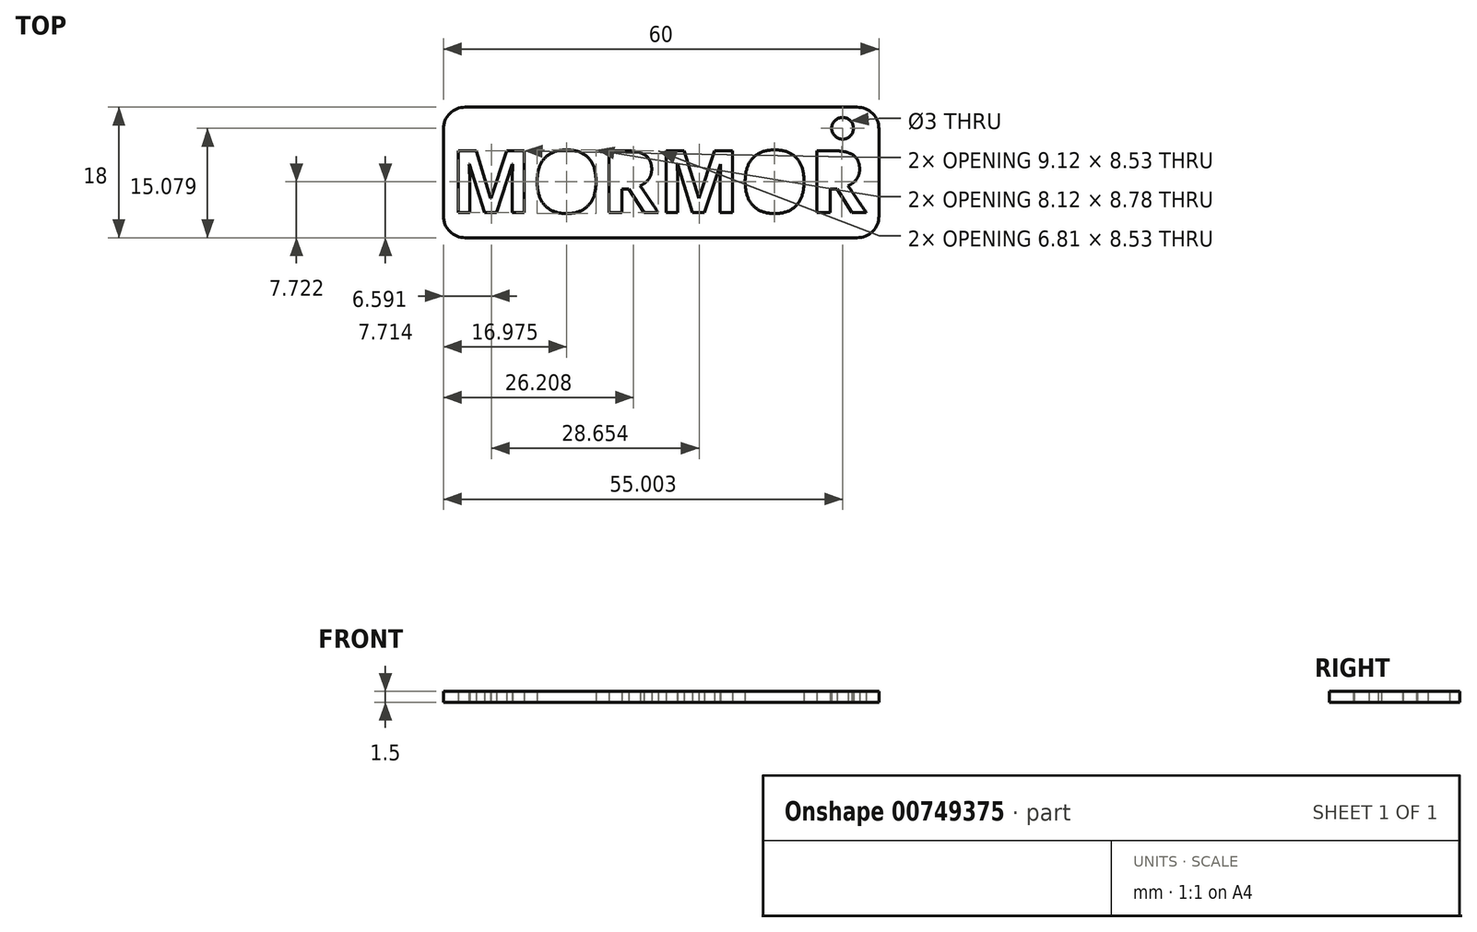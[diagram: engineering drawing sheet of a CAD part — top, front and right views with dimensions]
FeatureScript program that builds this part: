
annotation { "Feature Type Name" : "Feature", "Feature Type Description" : "" }
export const myFeature = defineFeature(function(context is Context, id is Id, definition is map)
    precondition{}
    {
        {
            var Q0;
            Q0=qCreatedBy(makeId("Top.planeOp"),FACE);
            var sketch = newSketch(context, id + "F0", { "sketchPlane" : qUnion([Q0])});
            skLineSegment(sketch, "E0.bottom", {"start": v(-26.45, -7.35) * mm, "end": v(33.55, -7.35) * mm});
            skLineSegment(sketch, "E0.top", {"start": v(-26.45, -25.35) * mm, "end": v(33.55, -25.35) * mm});
            skLineSegment(sketch, "E0.left", {"start": v(-26.45, -7.35) * mm, "end": v(-26.45, -25.35) * mm});
            skLineSegment(sketch, "E0.right", {"start": v(33.55, -7.35) * mm, "end": v(33.55, -25.35) * mm});
            skLineSegment(sketch, "E1", {"start": v(-21.45, -7.35) * mm, "end": v(-21.45, -25.35) * mm, "construction": true});
            skLineSegment(sketch, "E2", {"start": v(28.55, -7.35) * mm, "end": v(28.55, -25.35) * mm, "construction": true});
            skCircle(sketch, "E3", {"center": v(28.55, -10.27) * mm, "radius": 1.5 * mm});
            skText(sketch, "E4", { "text": "MORMOR", "fontName": "OpenSans-Bold.ttf"});
            skPoint(sketch, "E5", {"position": v(3.55, -25.35) * mm});
            const initialGuessF0  = {"E4": [-0.02549, -0.0219, 1, 0, 0.0086]};
            skSetInitialGuess(sketch, initialGuessF0);
            skSolve(sketch);
        }
        {
            var Q0;
            Q0=makeQuery(id+"F0.imprint","IMPRINT",FACE,{"disambiguationData":[TD([[makeQuery(id+"F0.imprint","IMPRINT",EDGE,{"derivedFrom":sQuery(id+"F0.wireOp",EDGE,"7f159fb4-957e-4c1e-b06f-ab5fa9d5e556.sketch_text.stroke-0")}),1.0]])]});
            var Q1;
            Q1=makeQuery(id+"F0.imprint","IMPRINT",FACE,{"disambiguationData":[TD([[makeQuery(id+"F0.imprint","IMPRINT",EDGE,{"derivedFrom":sQuery(id+"F0.wireOp",EDGE,"E0.bottom")}),-1.0]])]});
            extrude(context, id + "F1", {"entities" : qUnion([Q0, Q1]), "depth" : 1.5 * mm, "offsetDistance" : 25 * mm});
        }
        {
            var Q0;
            Q0=makeQuery(id+"F1.opExtrude","SWEPT_EDGE",EDGE,{"disambiguationData":[OSD([sQuery(id+"F0.wireOp",EDGE,"E0.top"),sQuery(id+"F0.wireOp",EDGE,"E0.right")])]});
            var Q1;
            Q1=makeQuery(id+"F1.opExtrude","SWEPT_EDGE",EDGE,{"disambiguationData":[OSD([sQuery(id+"F0.wireOp",EDGE,"E0.bottom"),sQuery(id+"F0.wireOp",EDGE,"E0.left")])]});
            var Q2;
            Q2=makeQuery(id+"F1.opExtrude","SWEPT_EDGE",EDGE,{"disambiguationData":[OSD([sQuery(id+"F0.wireOp",EDGE,"E0.bottom"),sQuery(id+"F0.wireOp",EDGE,"E0.right")])]});
            var Q3;
            Q3=makeQuery(id+"F1.opExtrude","SWEPT_EDGE",EDGE,{"disambiguationData":[OSD([sQuery(id+"F0.wireOp",EDGE,"E0.top"),sQuery(id+"F0.wireOp",EDGE,"E0.left")])]});
            fillet(context, id + "F2", {"entities" : qUnion([Q0, Q1, Q2, Q3]), "radius" : 3 * mm, "tangentPropagation" : true, "allowEdgeOverflow" : false});
        }
    });
